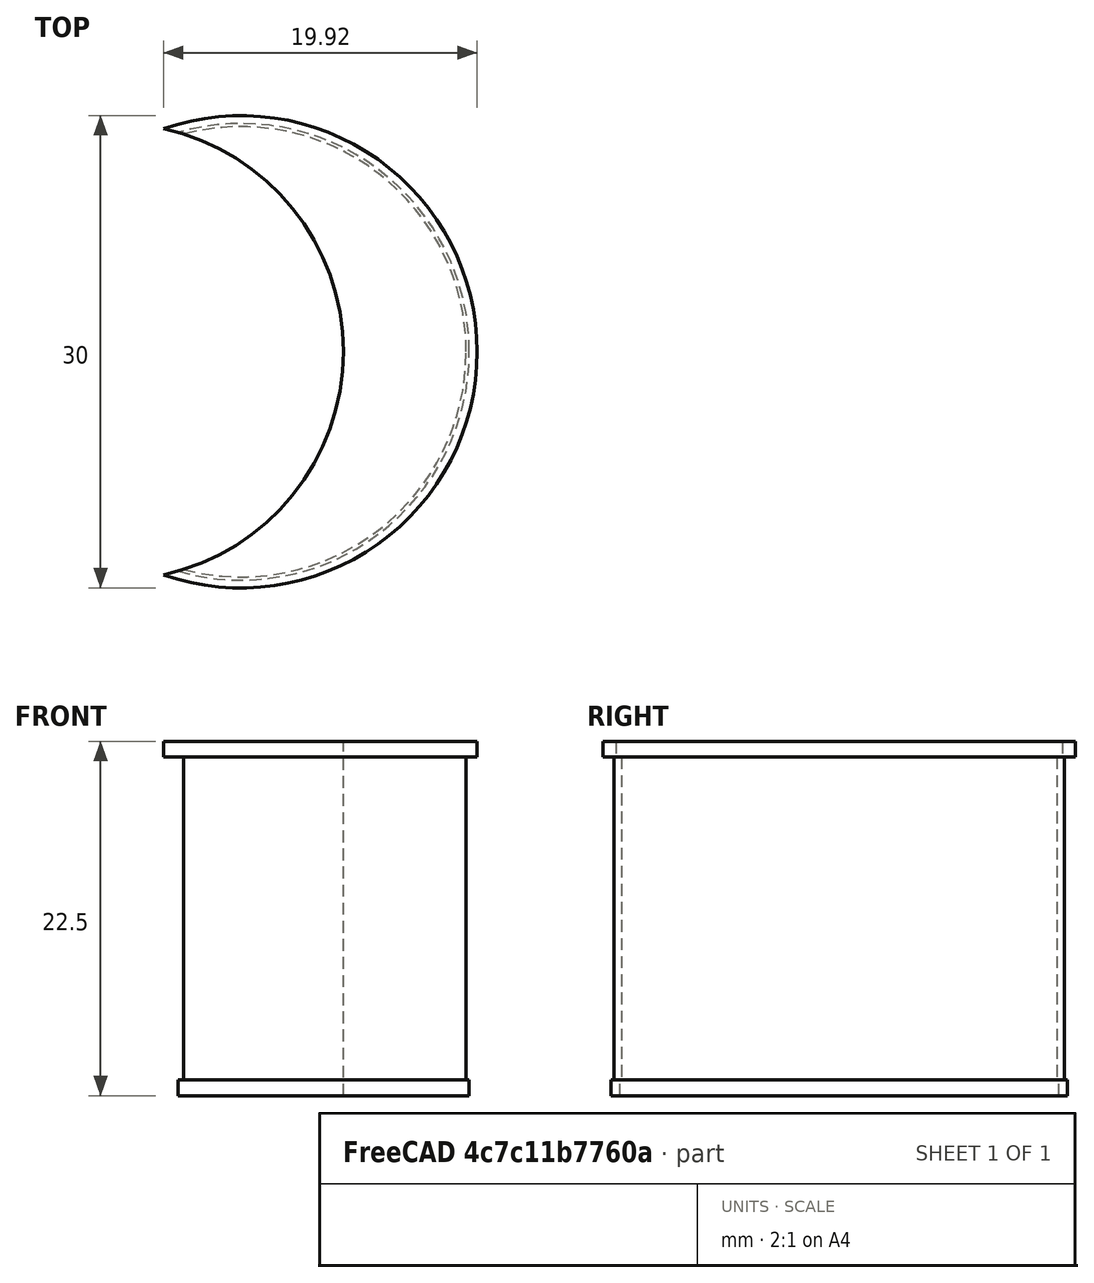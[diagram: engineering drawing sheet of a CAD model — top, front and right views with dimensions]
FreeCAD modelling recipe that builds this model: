
FCSTD DOCUMENT  (FreeCAD 0.19R)
Label: Spacer1
License: All rights reserved
LicenseURL: http://en.wikipedia.org/wiki/All_rights_reserved
objects: Sketcher::SketchObject×4, PartDesign::Pad×3, PartDesign::Pocket×1, PartDesign::Body×1, Mesh::Feature×1
note: 13 computed .brp shape members not serialized (recipe doc carries the construction recipe); baked Part::Feature solids carry a one-line shape summary decoded from their .brp

FEATURE [Sketcher::SketchObject] Sketch
  FullyConstrained = true
  MapMode = 5
  Support = -> [XY_Plane]
  sketch-geometry (1):
    g0: Circle CenterX=0 CenterY=0 CenterZ=0 NormalX=0 NormalY=0 NormalZ=1 AngleXU=0 Radius=14.3
  constraints (2):
    c: Diameter(g0) = 28.6
    c: Coincident(g0,g-1)
FEATURE [PartDesign::Pad] Pad
  Direction = (1,1,1)
  Length = 20.5
  Length2 = 100
  Profile = -> Sketch
  Type = 0
FEATURE [Sketcher::SketchObject] Sketch001
  FullyConstrained = true
  MapMode = 5
  Placement = pos=(0,0,20.5) rot=(0,0,1;0rad)
  Support = -> [Pad]
  sketch-geometry (1):
    g0: Circle CenterX=0 CenterY=0 CenterZ=0 NormalX=0 NormalY=0 NormalZ=1 AngleXU=0 Radius=15
  constraints (2):
    c: Coincident(g0,g-1)
    c: Diameter(g0) = 30
FEATURE [PartDesign::Pad] Pad001
  BaseFeature = -> Pad
  Direction = (1,1,1)
  Length = 1
  Length2 = 100
  Profile = -> Sketch001
  Type = 0
FEATURE [Sketcher::SketchObject] Sketch002
  FullyConstrained = true
  MapMode = 5
  Placement = pos=(0,0,0) rot=(1,0,0;3.14159rad)
  Support = -> [Pad001]
  sketch-geometry (1):
    g0: Circle CenterX=0 CenterY=0 CenterZ=0 NormalX=0 NormalY=0 NormalZ=1 AngleXU=0 Radius=14.5
  constraints (2):
    c: Coincident(g0,g-1)
    c: Diameter(g0) = 29
FEATURE [PartDesign::Pad] Pad002
  BaseFeature = -> Pad001
  Direction = (1,1,1)
  Length = 1
  Length2 = 100
  Profile = -> Sketch002
  Type = 0
FEATURE [Sketcher::SketchObject] Sketch003
  FullyConstrained = true
  MapMode = 5
  Placement = pos=(0,0,-1) rot=(1,0,0;3.14159rad)
  Support = -> [Pad002]
  sketch-geometry (1):
    g0: Circle CenterX=-8 CenterY=0 CenterZ=0 NormalX=0 NormalY=0 NormalZ=1 AngleXU=0 Radius=14.5
  constraints (3):
    c: PointOnObject(g0,g-1)
    c: Diameter(g0) = 29
    c: DistanceX(g0) = -8
FEATURE [PartDesign::Pocket] Pocket
  BaseFeature = -> Pad002
  Length = 5
  Length2 = 100
  Profile = -> Sketch003
  Type = 1
FEATURE [PartDesign::Body] Body
  Group = -> [Sketch,Pad,Sketch001,Pad001,Sketch002,Pad002,Sketch003,Pocket]
  Origin = -> Origin
  Tip = -> Pocket
FEATURE [Mesh::Feature] Mesh  label="Pocket (Meshed)"
